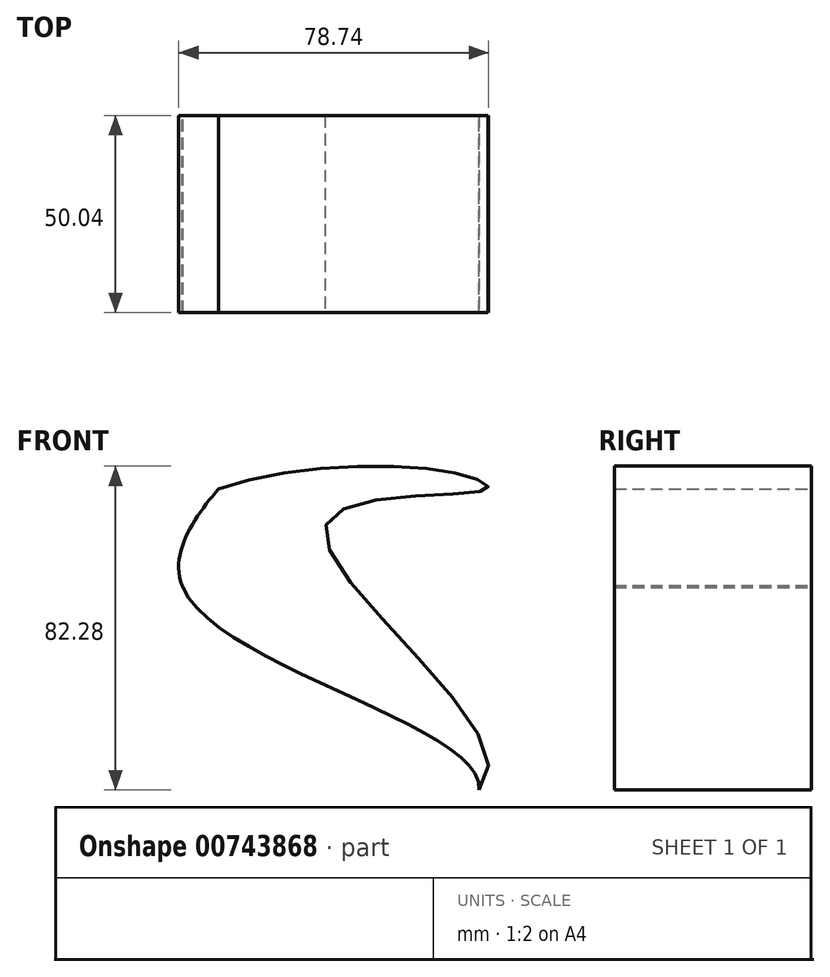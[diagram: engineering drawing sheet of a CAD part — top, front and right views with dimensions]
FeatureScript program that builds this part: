
annotation { "Feature Type Name" : "Feature", "Feature Type Description" : "" }
export const myFeature = defineFeature(function(context is Context, id is Id, definition is map)
    precondition{}
    {
        {
            var Q0;
            Q0=qCreatedBy(makeId("Front.planeOp"),FACE);
            var sketch = newSketch(context, id + "F0", { "sketchPlane" : qUnion([Q0])});
            skFitSpline(sketch, "E0", {"points": [v(79.19, 33.67) * mm, v(38.46, 24.8) * mm, v(79.64, -38.15) * mm, v(12.04, -40.3) * mm, v(4.62, 0) * mm, v(-2.3, 23.28) * mm, v(22.25, 36.87) * mm, v(73.84, 37.28) * mm, v(79.19, 33.67) * mm]});
            skFitSpline(sketch, "E1", {"points": [v(-52.28, -60.86) * mm, v(77.27, -42.61) * mm, v(1.87, 9.32) * mm, v(18.68, 42.74) * mm, v(4.68, 36.55) * mm, v(-52.28, -60.86) * mm]});
            skSolve(sketch);
        }
        {
            var Q0;
            {var subQ0=sQuery(id+"F0.wireOp",EDGE,"E1");var subQ1=sQuery(id+"F0.wireOp",EDGE,"E0");var subQ2=makeQuery(id+"F0.imprint","INTERSECT",VERTEX,{"disambiguationData":[OD(2.0)],"derivedFrom":[subQ1,subQ0]});Q0=makeQuery(id+"F0.imprint","IMPRINT",FACE,{"disambiguationData":[TD([[makeQuery(id+"F0.imprint","IMPRINT",EDGE,{"disambiguationData":[TD([[subQ2,-1.0]])],"derivedFrom":subQ1}),-1.0]])]});}
            extrude(context, id + "F1", {"entities" : qUnion([Q0]), "depth" : 50.04 * mm, "offsetDistance" : 25.4 * mm});
        }
    });
